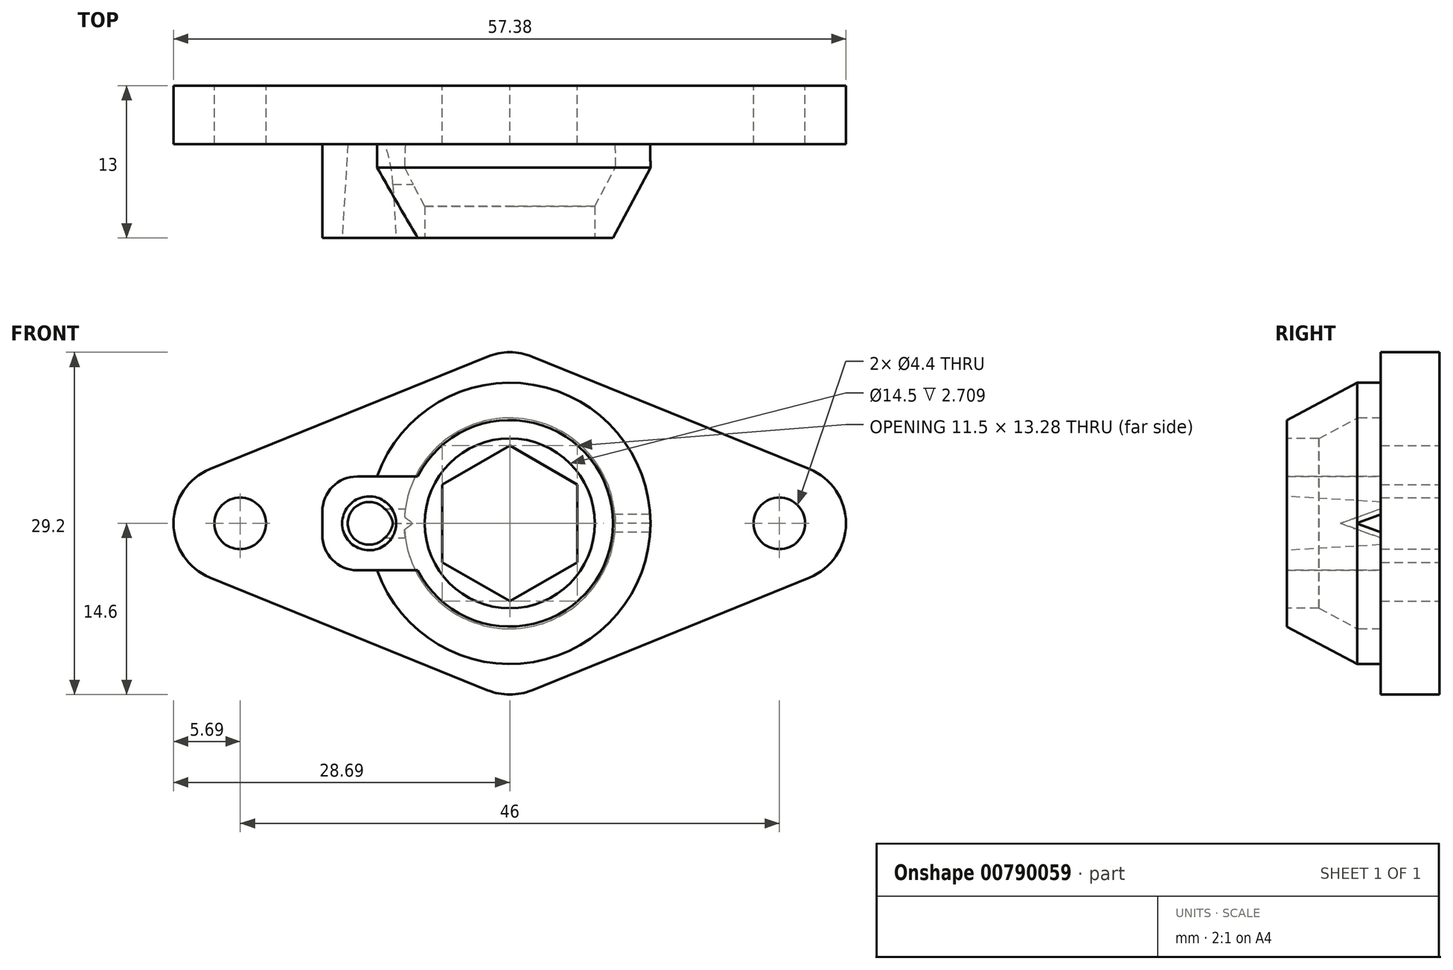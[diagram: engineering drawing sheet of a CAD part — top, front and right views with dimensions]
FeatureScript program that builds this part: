
annotation { "Feature Type Name" : "Feature", "Feature Type Description" : "" }
export const myFeature = defineFeature(function(context is Context, id is Id, definition is map)
    precondition{}
    {
        {
            var Q0;
            Q0=qCreatedBy(makeId("Front.planeOp"),FACE);
            var sketch = newSketch(context, id + "F0", { "sketchPlane" : qUnion([Q0])});
            skCircle(sketch, "E0", {"center": v(0, 0) * mm, "radius": 7 * mm, "construction": true});
            skCircle(sketch, "E1", {"center": v(-23, 0) * mm, "radius": 2.2 * mm});
            skCircle(sketch, "E2.MirrorC", {"center": v(23, 0) * mm, "radius": 2.2 * mm});
            skLineSegment(sketch, "E3", {"start": v(-25.57, 4.63) * mm, "end": v(-1.88, 14.24) * mm});
            skLineSegment(sketch, "E4.MirrorCS", {"start": v(-25.57, -4.63) * mm, "end": v(-1.88, -14.24) * mm});
            skLineSegment(sketch, "E5.MirrorCS", {"start": v(25.57, 4.63) * mm, "end": v(1.88, 14.24) * mm});
            skLineSegment(sketch, "E6.MirrorCS", {"start": v(25.57, -4.63) * mm, "end": v(1.88, -14.24) * mm});
            skPoint(sketch, "E7.visualSharp", {"position": v(0, 15) * mm});
            skArc(sketch, "E7.filletArc", {"start": v(1.88, 14.24) * mm, "mid": v(0, 14.6) * mm, "end": v(-1.88, 14.24) * mm});
            skPoint(sketch, "E8.visualSharp", {"position": v(-37, 0) * mm});
            skArc(sketch, "E8.filletArc", {"start": v(-25.57, 4.63) * mm, "mid": v(-28.7, 0) * mm, "end": v(-25.57, -4.63) * mm});
            skPoint(sketch, "E9.visualSharp", {"position": v(37, 0) * mm});
            skArc(sketch, "E9.filletArc", {"start": v(25.57, -4.63) * mm, "mid": v(28.7, 0) * mm, "end": v(25.57, 4.63) * mm});
            skPoint(sketch, "E10.visualSharp", {"position": v(0, -15) * mm});
            skArc(sketch, "E10.filletArc", {"start": v(-1.88, -14.24) * mm, "mid": v(0, -14.6) * mm, "end": v(1.88, -14.24) * mm});
            skCircle(sketch, "E11.cCircle", {"center": v(0, 0) * mm, "radius": 5.75 * mm, "construction": true});
            skLineSegment(sketch, "E11.0", {"start": v(5.75, 3.32) * mm, "end": v(5.75, -3.32) * mm});
            skLineSegment(sketch, "E11.1", {"start": v(5.75, -3.32) * mm, "end": v(0, -6.64) * mm});
            skLineSegment(sketch, "E11.2", {"start": v(0, -6.64) * mm, "end": v(-5.75, -3.32) * mm});
            skLineSegment(sketch, "E11.3", {"start": v(-5.75, -3.32) * mm, "end": v(-5.75, 3.32) * mm});
            skLineSegment(sketch, "E11.4", {"start": v(-5.75, 3.32) * mm, "end": v(0, 6.64) * mm});
            skLineSegment(sketch, "E11.5", {"start": v(0, 6.64) * mm, "end": v(5.75, 3.32) * mm});
            skPoint(sketch, "E11.0.midPoint", {"position": v(5.75, 0) * mm});
            skSolve(sketch);
        }
        {
            var Q0;
            Q0 = qSketchRegion(id + "F0", true);
            extrude(context, id + "F1", {"entities" : qUnion([Q0]), "depth" : 5 * mm, "offsetDistance" : 25 * mm});
        }
        {
            var Q0;
            Q0=qCreatedBy(makeId("Front.planeOp"),FACE);
            var sketch = newSketch(context, id + "F2", { "sketchPlane" : qUnion([Q0])});
            skCircle(sketch, "E12", {"center": v(0, 0) * mm, "radius": 7 * mm, "construction": true});
            skCircle(sketch, "E13", {"center": v(0, 0) * mm, "radius": 9 * mm});
            skCircle(sketch, "E14", {"center": v(0, 0) * mm, "radius": 12 * mm});
            skSolve(sketch);
        }
        {
            var Q0;
            Q0=qCreatedBy(makeId("Top.planeOp"),FACE);
            var sketch = newSketch(context, id + "F3", { "sketchPlane" : qUnion([Q0])});
            skLineSegment(sketch, "E15", {"start": v(-12, 0) * mm, "end": v(-9, 0) * mm});
            skLineSegment(sketch, "E16", {"start": v(-9, 0) * mm, "end": v(-9, -7) * mm});
            skLineSegment(sketch, "E17", {"start": v(-9, -7) * mm, "end": v(-7.25, -10.3) * mm});
            skLineSegment(sketch, "E18", {"start": v(-8.8, -13) * mm, "end": v(-7.25, -13) * mm});
            skLineSegment(sketch, "E19", {"start": v(-7.25, -13) * mm, "end": v(-7.25, -10.3) * mm});
            skLineSegment(sketch, "E20", {"start": v(0, -31.42) * mm, "end": v(0, 19) * mm, "construction": true});
            skLineSegment(sketch, "E21", {"start": v(-12, 0) * mm, "end": v(-12, -7) * mm});
            skLineSegment(sketch, "E22", {"start": v(-12, -7) * mm, "end": v(-8.8, -13) * mm});
            skSolve(sketch);
        }
        {
            var Q0;
            Q0 = qSketchRegion(id + "F3", true);
            var Q1;
            Q1=sQuery(id+"F3.wireOp",EDGE,"E20");
            revolve(context, id + "F4", {"operationType" : NewBodyOperationType.ADD, "surfaceOperationType" : NewSurfaceOperationType.NEW, "entities" : qUnion([Q0]), "axis" : qUnion([Q1]), "revolveType" : RevolveType.FULL});
        }
        {
            var Q0;
            {var subQ0=sQuery(id+"F0.wireOp",EDGE,"E9.filletArc");var subQ1=sQuery(id+"F0.wireOp",EDGE,"E8.filletArc");var subQ2=sQuery(id+"F0.wireOp",EDGE,"E7.filletArc");var subQ3=sQuery(id+"F0.wireOp",EDGE,"E6.MirrorCS");var subQ4=sQuery(id+"F0.wireOp",EDGE,"E5.MirrorCS");var subQ5=sQuery(id+"F0.wireOp",EDGE,"E10.filletArc");var subQ6=sQuery(id+"F0.wireOp",EDGE,"E1");var subQ7=sQuery(id+"F0.wireOp",EDGE,"E4.MirrorCS");var subQ8=sQuery(id+"F0.wireOp",EDGE,"E2.MirrorC");var subQ9=sQuery(id+"F0.wireOp",EDGE,"E3");Q0=makeQuery(id+"F4.boolean.opBoolean","SPLIT",FACE,{"disambiguationData":[TD([makeQuery(id+"F1.opExtrude","SWEPT_FACE",FACE,{"disambiguationData":[OSD([subQ6])]})])],"derivedFrom":makeQuery(id+"F1.opExtrude","CAP_FACE",FACE,{"disambiguationData":[OSD([subQ6,subQ8,subQ9,subQ7,subQ4,subQ3,subQ2,subQ1,subQ0,subQ5,sQuery(id+"F0.wireOp",EDGE,"E11.0"),sQuery(id+"F0.wireOp",EDGE,"E11.1"),sQuery(id+"F0.wireOp",EDGE,"E11.2"),sQuery(id+"F0.wireOp",EDGE,"E11.3"),sQuery(id+"F0.wireOp",EDGE,"E11.4"),sQuery(id+"F0.wireOp",EDGE,"E11.5")])],"isStart":false})});}
            var sketch = newSketch(context, id + "F5", { "sketchPlane" : qUnion([Q0])});
            skLineSegment(sketch, "E23", {"start": v(-16, 4) * mm, "end": v(-9, 4) * mm});
            skLineSegment(sketch, "E24.MirrorCS", {"start": v(-16, -4) * mm, "end": v(-9, -4) * mm});
            skLineSegment(sketch, "E25", {"start": v(-16, 4) * mm, "end": v(-16, -4) * mm});
            skLineSegment(sketch, "E26", {"start": v(-9, 4) * mm, "end": v(-9, -4) * mm});
            skSolve(sketch);
        }
        {
            var Q0;
            Q0 = qSketchRegion(id + "F5", true);
            extrude(context, id + "F6", {"entities" : qUnion([Q0]), "operationType" : NewBodyOperationType.ADD, "depth" : 8 * mm, "offsetDistance" : 25 * mm});
        }
        {
            var Q0;
            Q0=qCreatedBy(makeId("Top.planeOp"),FACE);
            var sketch = newSketch(context, id + "F7", { "sketchPlane" : qUnion([Q0])});
            skLineSegment(sketch, "E27", {"start": v(-12, 0) * mm, "end": v(-12, -19.6) * mm, "construction": true});
            skLineSegment(sketch, "E28.MirrorCS", {"start": v(-9.7, -13) * mm, "end": v(-10.18, -5) * mm});
            skLineSegment(sketch, "E29", {"start": v(-12, -5) * mm, "end": v(-10.18, -5) * mm});
            skLineSegment(sketch, "E30", {"start": v(-12, -13) * mm, "end": v(-9.7, -13) * mm});
            skPoint(sketch, "E31.start.orphan", {"position": v(-14.3, -13) * mm});
            skPoint(sketch, "E32.orphan", {"position": v(-13.82, -5) * mm});
            skLineSegment(sketch, "E33", {"start": v(-12, -5) * mm, "end": v(-12, -13) * mm});
            skLineSegment(sketch, "E34", {"start": v(-9.7, -13) * mm, "end": v(-9.7, -6.54) * mm, "construction": true});
            skSolve(sketch);
        }
        {
            var Q0;
            Q0=makeQuery(id+"F7.imprint","IMPRINT",FACE,{"disambiguationData":[TD([[makeQuery(id+"F7.imprint","IMPRINT",EDGE,{"derivedFrom":sQuery(id+"F7.wireOp",EDGE,"E28.MirrorCS")}),1.0]])]});
            var Q1;
            Q1=sQuery(id+"F7.wireOp",EDGE,"E27");
            revolve(context, id + "F8", {"operationType" : NewBodyOperationType.REMOVE, "surfaceOperationType" : NewSurfaceOperationType.NEW, "entities" : qUnion([Q0]), "axis" : qUnion([Q1]), "revolveType" : RevolveType.FULL});
        }
        {
            var Q0;
            Q0=makeQuery(id+"F1.opExtrude","SWEPT_FACE",FACE,{"disambiguationData":[OSD([sQuery(id+"F0.wireOp",EDGE,"E11.3")])]});
            var sketch = newSketch(context, id + "F9", { "sketchPlane" : qUnion([Q0])});
            skLineSegment(sketch, "E35", {"start": v(-5, -1.25) * mm, "end": v(-8.43, 0) * mm});
            skLineSegment(sketch, "E36.MirrorCS", {"start": v(-5, 1.25) * mm, "end": v(-8.43, 0) * mm});
            skLineSegment(sketch, "E37", {"start": v(-5, 1.25) * mm, "end": v(-5, -1.25) * mm});
            skSolve(sketch);
        }
        {
            var Q0;
            Q0 = qSketchRegion(id + "F9", true);
            extrude(context, id + "F10", {"entities" : qUnion([Q0]), "operationType" : NewBodyOperationType.REMOVE, "oppositeDirection" : true, "depth" : 7 * mm, "offsetDistance" : 25 * mm});
        }
        {
            var Q0;
            Q0=makeQuery(id+"F1.opExtrude","SWEPT_FACE",FACE,{"disambiguationData":[OSD([sQuery(id+"F0.wireOp",EDGE,"E11.0")])]});
            var sketch = newSketch(context, id + "F11", { "sketchPlane" : qUnion([Q0])});
            skLineSegment(sketch, "E38", {"start": v(5, 0.75) * mm, "end": v(7.06, 0) * mm});
            skLineSegment(sketch, "E39.MirrorCS", {"start": v(5, -0.75) * mm, "end": v(7.06, 0) * mm});
            skLineSegment(sketch, "E40", {"start": v(5, 0.75) * mm, "end": v(5, -0.75) * mm});
            skSolve(sketch);
        }
        {
            var Q0;
            Q0 = qSketchRegion(id + "F11", true);
            extrude(context, id + "F12", {"entities" : qUnion([Q0]), "operationType" : NewBodyOperationType.REMOVE, "endBound" : BoundingType.THROUGH_ALL, "oppositeDirection" : true, "depth" : 25 * mm, "offsetDistance" : 25 * mm});
        }
        {
            var Q0;
            Q0=makeQuery(id+"F6.opExtrude","SWEPT_FACE",FACE,{"disambiguationData":[OSD([sQuery(id+"F5.wireOp",EDGE,"E26")])]});
            var sketch = newSketch(context, id + "F13", { "sketchPlane" : qUnion([Q0])});
            skLineSegment(sketch, "E41", {"start": v(-13, 4) * mm, "end": v(-11.05, 4) * mm});
            skLineSegment(sketch, "E42", {"start": v(-11.05, 4) * mm, "end": v(-11.05, -4) * mm});
            skLineSegment(sketch, "E43", {"start": v(-11.05, -4) * mm, "end": v(-13, -4) * mm});
            skLineSegment(sketch, "E44", {"start": v(-13, -4) * mm, "end": v(-13, 4) * mm});
            skSolve(sketch);
        }
        {
            var Q0;
            Q0 = qSketchRegion(id + "F13", true);
            extrude(context, id + "F14", {"entities" : qUnion([Q0]), "operationType" : NewBodyOperationType.ADD, "depth" : 1.5 * mm, "offsetDistance" : 25 * mm});
        }
        {
            var Q0;
            Q0=makeQuery(id+"F6.opExtrude","SWEPT_EDGE",EDGE,{"disambiguationData":[OSD([sQuery(id+"F5.wireOp",EDGE,"E24.MirrorCS"),sQuery(id+"F5.wireOp",EDGE,"E25")])]});
            fillet(context, id + "F15", {"entities" : qUnion([Q0]), "radius" : 3 * mm, "tangentPropagation" : true, "allowEdgeOverflow" : false});
        }
        {
            var Q0;
            Q0=makeQuery(id+"F6.opExtrude","SWEPT_EDGE",EDGE,{"disambiguationData":[OSD([sQuery(id+"F5.wireOp",EDGE,"E23"),sQuery(id+"F5.wireOp",EDGE,"E25")])]});
            fillet(context, id + "F16", {"entities" : qUnion([Q0]), "radius" : 3 * mm, "tangentPropagation" : true, "allowEdgeOverflow" : false});
        }
    });
